# Revit family: TEMID_Турникет_полноростовой_FHT2300
name_source: partatom
category: Охранная сигнализация
units: mm (PartAtom-declared; Revit-internal decimal feet)

## family parameters
Всегда вертикально = Нет
На основе рабочей плоскости = Нет
Общий = Да
При загрузке вырезать с полостями = Нет
Размер круглого соединителя = Использовать диаметр
Сохранять ориентацию аннотаций = Нет
Тип детали = Нормальный
Точка расчета площади = Да

## types (1)
- FHT2300
    =Габариты= = =Габариты=
    ADSK_Единица измерения = шт.
    ADSK_Завод-изготовитель = TEMID
    ADSK_Классификация нагрузок = Прочее
    ADSK_Количество = 1
    ADSK_Количество фаз = 1
    ADSK_Коэффициент мощности = 1
    ADSK_Марка = FHT2300
    ADSK_Наименование = Турникет полноростовой 3-х лопастной (120°). Ширина прохода 580 мм. Материал корпуса - нержавеющая сталь SUS304. Материал преграждающих планок - нержавеющая сталь SUS304. Светодиодный индикатор прохода. Установка внутренняя / наружняя (под навесом). Степень защиты IP54. Рабочая температура -28 °C  -  60 °C. Размер, мм 1400х1395х2220. Питание 200 ~ 240V. Наработка на отказ 2 млн. проходов.
    ADSK_Напряжение = 220 В
    ADSK_Номинальная мощность = 120 Вт
    ADSK_Обозначение = RD
    ADSK_Полная мощность = 120 В·А
    ADSK_Раздел спецификации = 3. Периферийное оборудование
    ADSK_Размер_Высота = 2220 мм
    ADSK_Размер_Глубина = 1400 мм
    ADSK_Размер_Ширина = 1395 мм
    ADSK_Тип = FHT2300
    ADSK_Ток = 545.455 мА
    URL = https://temid-global.ru
    Материал = Серый
    Отметка по умолчанию = 0 мм
    Трипод_Диаметр = 40 мм
